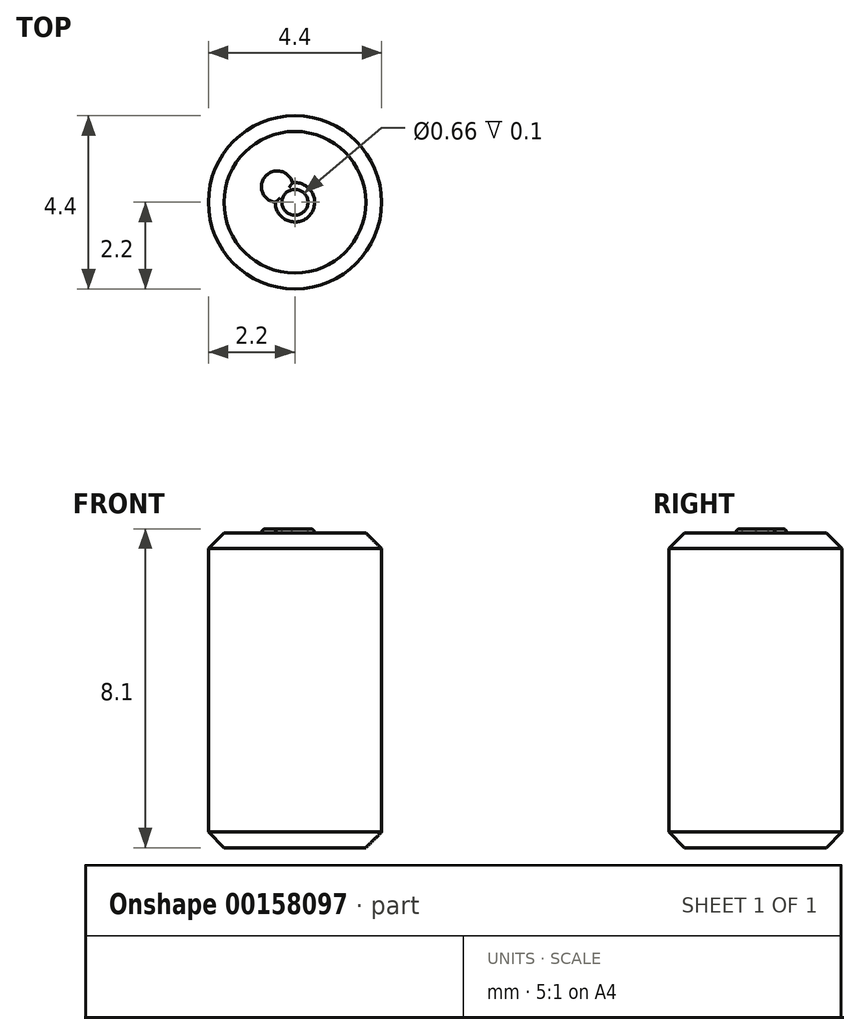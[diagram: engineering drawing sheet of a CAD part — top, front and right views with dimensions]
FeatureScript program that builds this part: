
annotation { "Feature Type Name" : "Feature", "Feature Type Description" : "" }
export const myFeature = defineFeature(function(context is Context, id is Id, definition is map)
    precondition{}
    {
        {
            var Q0;
            Q0=qCreatedBy(makeId("Top.planeOp"),FACE);
            var sketch = newSketch(context, id + "F0", { "sketchPlane" : qUnion([Q0])});
            skCircle(sketch, "E0", {"center": v(0, 0) * mm, "radius": 2.2 * mm});
            skSolve(sketch);
        }
        {
            var Q0;
            Q0=makeQuery(id+"F0.imprint","IMPRINT",FACE,{"disambiguationData":[TD([[makeQuery(id+"F0.imprint","IMPRINT",EDGE,{"derivedFrom":sQuery(id+"F0.wireOp",EDGE,"E0")}),1.0]])]});
            extrude(context, id + "F1", {"entities" : qUnion([Q0]), "depth" : 8 * mm});
        }
        {
            var Q0;
            Q0=makeQuery(id+"F1.opExtrude","CAP_EDGE",EDGE,{"disambiguationData":[OSD([sQuery(id+"F0.wireOp",EDGE,"E0")])],"isStart":false});
            chamfer(context, id + "F2", {"entities" : qUnion([Q0]), "width" : 0.4 * mm, "tangentPropagation" : true});
        }
        {
            var Q0;
            Q0=makeQuery(id+"F1.opExtrude","CAP_EDGE",EDGE,{"disambiguationData":[OSD([sQuery(id+"F0.wireOp",EDGE,"E0")])],"isStart":true});
            chamfer(context, id + "F3", {"entities" : qUnion([Q0]), "width" : 0.4 * mm, "tangentPropagation" : true});
        }
        {
            var Q0;
            Q0=makeQuery(id+"F1.opExtrude","CAP_FACE",FACE,{"disambiguationData":[OSD([sQuery(id+"F0.wireOp",EDGE,"E0")])],"isStart":false});
            var sketch = newSketch(context, id + "F4", { "sketchPlane" : qUnion([Q0])});
            skArc(sketch, "E1", {"start": v(-0.5, 0) * mm, "mid": v(0.37, -0.33) * mm, "end": v(-0.06, 0.5) * mm});
            skLineSegment(sketch, "E2", {"start": v(0, 0) * mm, "end": v(-1.09, 0.96) * mm, "construction": true});
            skArc(sketch, "E3", {"start": v(-0.06, 0.5) * mm, "mid": v(-0.75, 0.66) * mm, "end": v(-0.5, 0) * mm});
            skSolve(sketch);
        }
        {
            var Q0;
            Q0=makeQuery(id+"F4.imprint","IMPRINT",FACE,{"disambiguationData":[TD([[makeQuery(id+"F4.imprint","IMPRINT",EDGE,{"derivedFrom":sQuery(id+"F4.wireOp",EDGE,"E1")}),1.0]])]});
            extrude(context, id + "F5", {"entities" : qUnion([Q0]), "operationType" : NewBodyOperationType.ADD, "depth" : 0.1 * mm});
        }
        {
            var Q0;
            Q0=makeQuery(id+"F5.opExtrude","CAP_FACE",FACE,{"disambiguationData":[OSD([sQuery(id+"F4.wireOp",EDGE,"E1"),sQuery(id+"F4.wireOp",EDGE,"E3")])],"isStart":false});
            var sketch = newSketch(context, id + "F6", { "sketchPlane" : qUnion([Q0])});
            skCircle(sketch, "E4", {"center": v(0, 0) * mm, "radius": 0.33 * mm});
            skSolve(sketch);
        }
        {
            var Q0;
            Q0=makeQuery(id+"F6.imprint","IMPRINT",FACE,{"disambiguationData":[TD([[makeQuery(id+"F6.imprint","IMPRINT",EDGE,{"derivedFrom":sQuery(id+"F6.wireOp",EDGE,"E4")}),1.0]])]});
            extrude(context, id + "F7", {"entities" : qUnion([Q0]), "operationType" : NewBodyOperationType.REMOVE, "oppositeDirection" : true, "depth" : 0.1 * mm});
        }
        {
            var Q0;
            Q0=makeQuery(id+"F5.opExtrude","CAP_EDGE",EDGE,{"disambiguationData":[OSD([sQuery(id+"F4.wireOp",EDGE,"E3")])],"isStart":false});
            var Q1;
            Q1=makeQuery(id+"F5.opExtrude","CAP_EDGE",EDGE,{"disambiguationData":[OSD([sQuery(id+"F4.wireOp",EDGE,"E1")])],"isStart":false});
            var Q2;
            Q2=makeQuery(id+"F7.boolean.opBoolean","COPY",EDGE,{"derivedFrom":makeQuery(id+"F7.opExtrude","CAP_EDGE",EDGE,{"disambiguationData":[OSD([sQuery(id+"F6.wireOp",EDGE,"E4")])],"isStart":true})});
            fillet(context, id + "F8", {"entities" : qUnion([Q0, Q1, Q2]), "radius" : 0.1 * mm, "tangentPropagation" : true, "allowEdgeOverflow" : false});
        }
    });
